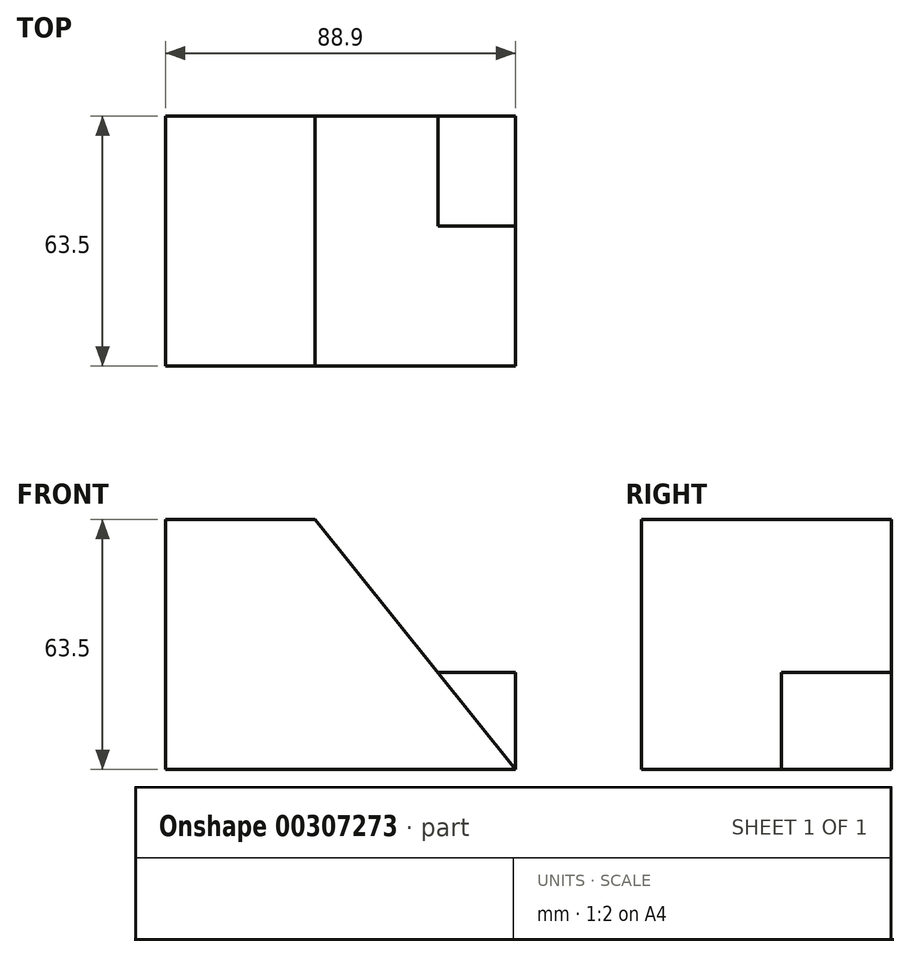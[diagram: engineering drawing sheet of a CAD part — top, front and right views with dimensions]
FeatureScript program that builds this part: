
annotation { "Feature Type Name" : "Feature", "Feature Type Description" : "" }
export const myFeature = defineFeature(function(context is Context, id is Id, definition is map)
    precondition{}
    {
        {
            var Q0;
            Q0=qCreatedBy(makeId("Top.planeOp"),FACE);
            var sketch = newSketch(context, id + "F0", { "sketchPlane" : qUnion([Q0])});
            skLineSegment(sketch, "E0", {"start": v(-46.18, -44.67) * mm, "end": v(42.72, -44.67) * mm});
            skLineSegment(sketch, "E1", {"start": v(42.72, -44.67) * mm, "end": v(42.72, 18.83) * mm});
            skLineSegment(sketch, "E2", {"start": v(42.72, 18.83) * mm, "end": v(-46.18, 18.83) * mm});
            skLineSegment(sketch, "E3", {"start": v(-46.18, 18.83) * mm, "end": v(-46.18, -44.67) * mm});
            skSolve(sketch);
        }
        {
            var Q0;
            Q0=makeQuery(id+"F0.imprint","IMPRINT",FACE,{"disambiguationData":[TD([[makeQuery(id+"F0.imprint","IMPRINT",EDGE,{"derivedFrom":sQuery(id+"F0.wireOp",EDGE,"E0")}),1.0]])]});
            extrude(context, id + "F1", {"entities" : qUnion([Q0]), "depth" : 63.5 * mm});
        }
        {
            var Q0;
            Q0=makeQuery(id+"F1.opExtrude","SWEPT_FACE",FACE,{"disambiguationData":[OSD([sQuery(id+"F0.wireOp",EDGE,"E0")])]});
            var sketch = newSketch(context, id + "F2", { "sketchPlane" : qUnion([Q0])});
            skLineSegment(sketch, "E4", {"start": v(-46.18, 63.5) * mm, "end": v(-8.15, 63.5) * mm});
            skLineSegment(sketch, "E5", {"start": v(-8.15, 63.5) * mm, "end": v(42.72, 0) * mm});
            skLineSegment(sketch, "E6", {"start": v(42.72, 0) * mm, "end": v(42.72, 63.5) * mm});
            skLineSegment(sketch, "E7", {"start": v(42.72, 63.5) * mm, "end": v(-8.15, 63.5) * mm});
            skSolve(sketch);
        }
        {
            var Q0;
            Q0=makeQuery(id+"F2.imprint","IMPRINT",FACE,{"disambiguationData":[TD([[makeQuery(id+"F2.imprint","IMPRINT",EDGE,{"derivedFrom":sQuery(id+"F2.wireOp",EDGE,"E5")}),1.0]])]});
            extrude(context, id + "F3", {"entities" : qUnion([Q0]), "operationType" : NewBodyOperationType.REMOVE, "endBound" : BoundingType.THROUGH_ALL, "oppositeDirection" : true, "depth" : 25.4 * mm});
        }
        {
            var Q0;
            Q0=makeQuery(id+"F3.boolean.opBoolean","COPY",FACE,{"derivedFrom":makeQuery(id+"F3.opExtrude","SWEPT_FACE",FACE,{"disambiguationData":[OSD([sQuery(id+"F2.wireOp",EDGE,"E5")])]})});
            var sketch = newSketch(context, id + "F4", { "sketchPlane" : qUnion([Q0])});
            skLineSegment(sketch, "E8", {"start": v(-19.27, -26.71) * mm, "end": v(-19.27, 0) * mm});
            skLineSegment(sketch, "E9", {"start": v(-19.27, 0) * mm, "end": v(18.83, 0) * mm});
            skSolve(sketch);
        }
        {
            var Q0;
            {var subQ0=sQuery(id+"F4.wireOp",EDGE,"E8");Q0=makeQuery(id+"F4.imprint","IMPRINT",FACE,{"disambiguationData":[TD([[makeQuery(id+"F4.imprint","IMPRINT",EDGE,{"derivedFrom":subQ0}),-1.0]])]});}
            extrude(context, id + "F5", {"entities" : qUnion([Q0]), "operationType" : NewBodyOperationType.ADD, "depth" : 25.4 * mm});
        }
        {
            var Q0;
            Q0=makeQuery(id+"F5.opExtrude","SWEPT_FACE",FACE,{"disambiguationData":[OSD([sQuery(id+"F4.wireOp",EDGE,"E9")])]});
            var sketch = newSketch(context, id + "F6", { "sketchPlane" : qUnion([Q0])});
            skSolve(sketch);
        }
        {
            var Q0;
            {var subQ0=sQuery(id+"F4.wireOp",EDGE,"E9");var subQ1=makeQuery(id+"F5.opExtrude","CAP_EDGE",EDGE,{"disambiguationData":[OSD([subQ0])],"isStart":false});Q0=makeQuery(id+"F6.imprint","IMPRINT",FACE,{"disambiguationData":[TD([[makeQuery(id+"F6.imprint","IMPRINT",EDGE,{"derivedFrom":subQ1}),1.0]])]});}
            extrude(context, id + "F7", {"entities" : qUnion([Q0]), "operationType" : NewBodyOperationType.REMOVE, "oppositeDirection" : true, "depth" : 40.13 * mm});
        }
        {
            var Q0;
            {var subQ0=sQuery(id+"F0.wireOp",EDGE,"E2");Q0=makeQuery(id+"F5.boolean.opBoolean","MERGE",FACE,{"derivedFrom":[makeQuery(id+"F1.opExtrude","SWEPT_FACE",FACE,{"disambiguationData":[OSD([subQ0])]}),makeQuery(id+"F5.opExtrude","SWEPT_FACE",FACE,{"disambiguationData":[OSD([subQ0,sQuery(id+"F2.wireOp",EDGE,"E5")])]})]});}
            var sketch = newSketch(context, id + "F8", { "sketchPlane" : qUnion([Q0])});
            skLineSegment(sketch, "E10", {"start": v(-23, 24.63) * mm, "end": v(-42.72, 24.63) * mm});
            skLineSegment(sketch, "E11", {"start": v(-42.72, 24.63) * mm, "end": v(-42.72, 0) * mm});
            skLineSegment(sketch, "E12", {"start": v(-42.72, 0) * mm, "end": v(-23, 24.63) * mm});
            skSolve(sketch);
        }
        {
            var Q0;
            Q0=makeQuery(id+"F8.imprint","IMPRINT",FACE,{"disambiguationData":[TD([[makeQuery(id+"F8.imprint","IMPRINT",EDGE,{"derivedFrom":sQuery(id+"F8.wireOp",EDGE,"E10")}),1.0]])]});
            extrude(context, id + "F9", {"entities" : qUnion([Q0]), "operationType" : NewBodyOperationType.ADD, "oppositeDirection" : true, "depth" : 27.94 * mm});
        }
    });
